# Revit family: Faucet_Bathroom-DXV-Rem-D3510010X_Series
name_source: partatom
category: Plumbing Fixtures
units: mm (PartAtom-declared; Revit-internal decimal feet)

## family parameters
Always vertical = No
Cut with Voids When Loaded = No
OmniClass Number = 23.45.55.14
OmniClass Title = Single Faucets
Part Type = Normal
Room Calculation Point = No
Round Connector Dimension = Use Diameter
Shared = Yes
Work Plane-Based = Yes

## types (4) — shared parameters
ADA Compliant = Yes
Assembly Code = D2020300
CW Connection = No
CWFU = 1.5
CalGreen Compliant = Yes
Default Elevation = 0"
Description = Rem Widespread Lavatory Faucet
HW Connection = No
HWFU = 1.5
Height = 7 1/8"
IAPMO Compliance = Meets or Exceeds ASME A112.18.1/CSA B125.1/NSF 61/Section 9 and EPA WaterSense® High Efficiency
Installation Type = Deck Mounted
Length = 5 3/4"
Manufacturer = DXV
Price = Prices may vary. Please consult Manufacturer Representative for most up-to-date price list.
Product Documentation Link = https://dxv01.blob.core.windows.net
Product Page URL = https://www.dxv.com
Tempered Water Connection = Yes
Tempered Water Connection Diameter = 3/8"
URL = http://www.dxv.com
Vent Connection = No
WFU = 2
Waste Connection = No
Width = 1 1/2"

## per-type parameters (varying)
| type | Finish | Flow Rate | Material |
| D35100100.144 | Brass-DXV-144-Brushed Nickel | 1.5 GPM (5.7L/min) | Brass-DXV-144-Brushed Nickel |
| D3510010C.100 | Brass-DXV-100-Polished Chrome | 1.2 GPM (4.5 L/min) | Brass-DXV-100-Polished Chrome |
| D35100100.100 | Brass-DXV-100-Polished Chrome | 1.5 GPM (5.7L/min) | Brass-DXV-100-Polished Chrome |
| D3510010C.144 | Brass-DXV-100-Polished Chrome | 1.2 GPM (4.5 L/min) | Brass-DXV-100-Polished Chrome |

note: column(s) folded — value = type name in every type: Model

## geometry (parser evidence)
native form markers: Sweep x2
no freeform markers — native parametric forms only
